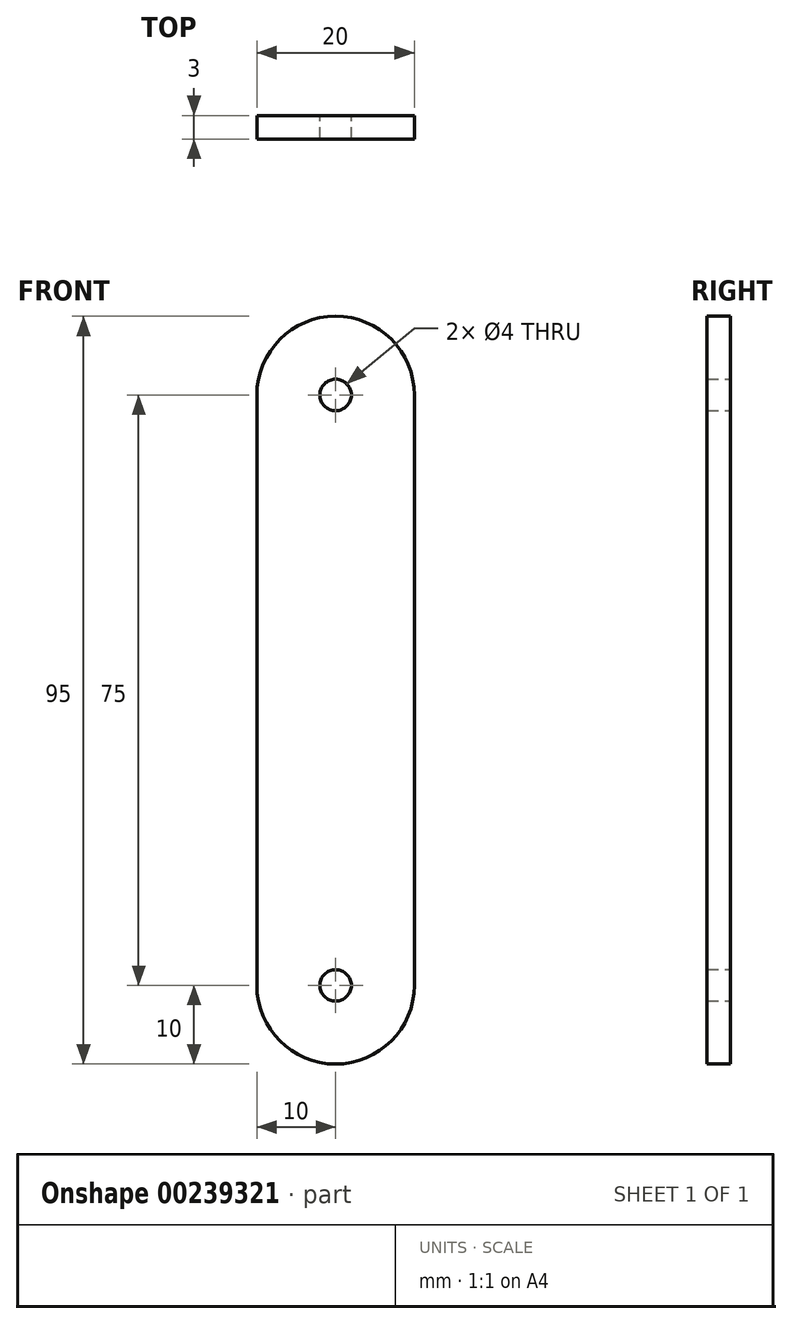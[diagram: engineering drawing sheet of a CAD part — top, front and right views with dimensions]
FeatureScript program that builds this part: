
annotation { "Feature Type Name" : "Feature", "Feature Type Description" : "" }
export const myFeature = defineFeature(function(context is Context, id is Id, definition is map)
    precondition{}
    {
        {
            var Q0;
            Q0=qCreatedBy(makeId("Front.planeOp"),FACE);
            var sketch = newSketch(context, id + "F0", { "sketchPlane" : qUnion([Q0])});
            skLineSegment(sketch, "E0.bottom", {"start": v(10, -37.5) * mm, "end": v(-10, -37.5) * mm, "construction": true});
            skLineSegment(sketch, "E0.top", {"start": v(10, 37.5) * mm, "end": v(-10, 37.5) * mm, "construction": true});
            skPoint(sketch, "E0.middle", {"position": v(0, 0) * mm});
            skArc(sketch, "E1", {"start": v(10, 37.5) * mm, "mid": v(0, 47.5) * mm, "end": v(-10, 37.5) * mm});
            skArc(sketch, "E2", {"start": v(-10, -37.5) * mm, "mid": v(0, -47.5) * mm, "end": v(10, -37.5) * mm});
            skCircle(sketch, "E3", {"center": v(0, 37.5) * mm, "radius": 2 * mm});
            skCircle(sketch, "E4", {"center": v(0, -37.5) * mm, "radius": 2 * mm});
            skLineSegment(sketch, "E5", {"start": v(-10, 37.5) * mm, "end": v(-10, -37.5) * mm});
            skLineSegment(sketch, "E6", {"start": v(10, 37.5) * mm, "end": v(10, -37.5) * mm});
            skSolve(sketch);
        }
        {
            var Q0;
            Q0 = qSketchRegion(id + "F0", true);
            extrude(context, id + "F1", {"entities" : qUnion([Q0]), "depth" : 3 * mm});
        }
    });
